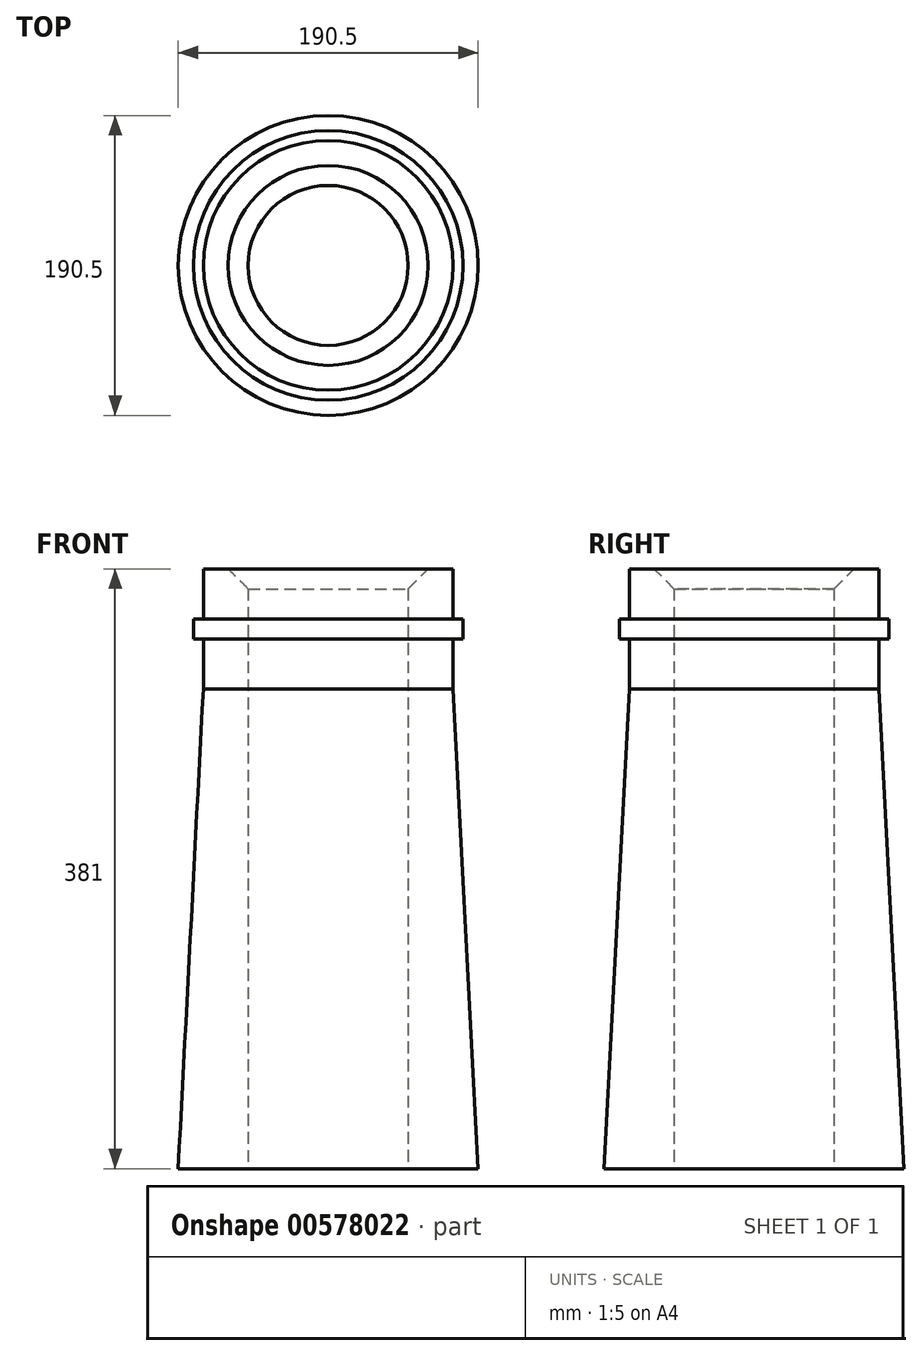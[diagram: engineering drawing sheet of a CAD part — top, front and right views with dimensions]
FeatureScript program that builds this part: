
annotation { "Feature Type Name" : "Feature", "Feature Type Description" : "" }
export const myFeature = defineFeature(function(context is Context, id is Id, definition is map)
    precondition{}
    {
        {
            var Q0;
            Q0=qCreatedBy(makeId("Front.planeOp"),FACE);
            var sketch = newSketch(context, id + "F0", { "sketchPlane" : qUnion([Q0])});
            skLineSegment(sketch, "E0", {"start": v(-95.25, 0) * mm, "end": v(-79.28, 304.8) * mm});
            skLineSegment(sketch, "E1", {"start": v(-79.28, 304.8) * mm, "end": v(-79.28, 336.55) * mm});
            skLineSegment(sketch, "E2", {"start": v(-79.28, 336.55) * mm, "end": v(-85.63, 336.55) * mm});
            skLineSegment(sketch, "E3", {"start": v(-85.63, 336.55) * mm, "end": v(-85.63, 349.25) * mm});
            skLineSegment(sketch, "E4", {"start": v(-85.63, 349.25) * mm, "end": v(-79.28, 349.25) * mm});
            skLineSegment(sketch, "E5", {"start": v(-79.28, 349.25) * mm, "end": v(-79.28, 381) * mm});
            skLineSegment(sketch, "E6", {"start": v(-79.28, 381) * mm, "end": v(-63.5, 381) * mm});
            skLineSegment(sketch, "E7", {"start": v(-63.5, 381) * mm, "end": v(-50.8, 368.3) * mm});
            skLineSegment(sketch, "E8", {"start": v(-50.8, 368.3) * mm, "end": v(-50.8, 0) * mm});
            skLineSegment(sketch, "E9", {"start": v(-50.8, 0) * mm, "end": v(-95.25, 0) * mm});
            skSolve(sketch);
        }
        {
            var Q0;
            Q0=qCreatedBy(makeId("Front.planeOp"),FACE);
            var sketch = newSketch(context, id + "F1", { "sketchPlane" : qUnion([Q0])});
            skLineSegment(sketch, "E10", {"start": v(0, -55.85) * mm, "end": v(0, 291.45) * mm, "construction": true});
            skSolve(sketch);
        }
        {
            var Q0;
            Q0 = qSketchRegion(id + "F0", true);
            var Q1;
            Q1=sQuery(id+"F1.wireOp",EDGE,"E10");
            revolve(context, id + "F2", {"entities" : qUnion([Q0]), "axis" : qUnion([Q1]), "revolveType" : RevolveType.FULL});
        }
    });
